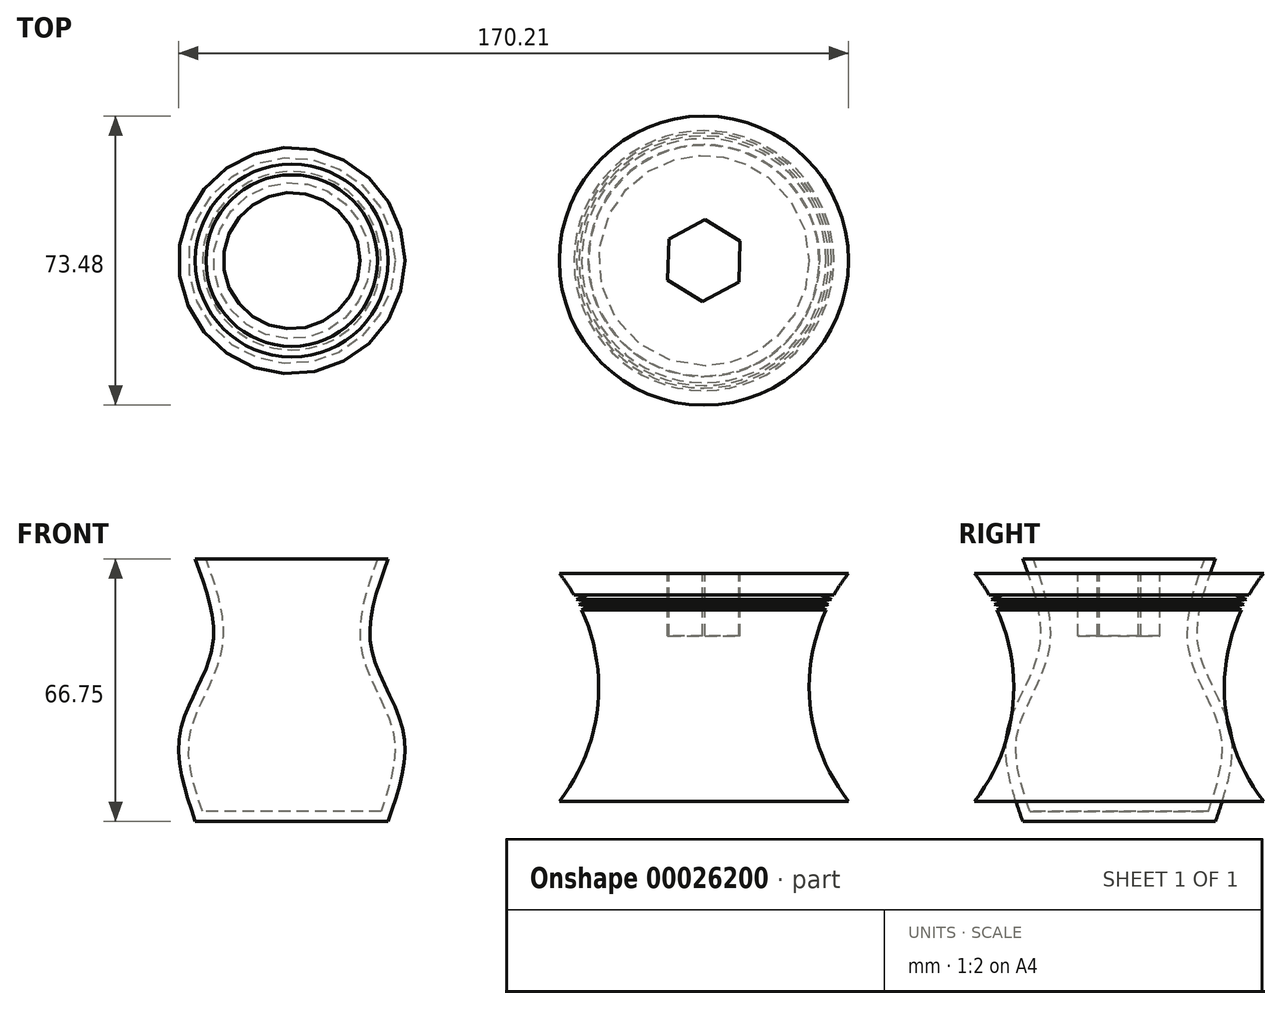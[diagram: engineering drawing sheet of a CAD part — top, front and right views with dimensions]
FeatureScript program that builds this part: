
annotation { "Feature Type Name" : "Feature", "Feature Type Description" : "" }
export const myFeature = defineFeature(function(context is Context, id is Id, definition is map)
    precondition{}
    {
        {
            var Q0;
            Q0=qCreatedBy(makeId("Front.planeOp"),FACE);
            var sketch = newSketch(context, id + "F0", { "sketchPlane" : qUnion([Q0])});
            skLineSegment(sketch, "E0", {"start": v(0, 26.32) * mm, "end": v(-36.74, 26.32) * mm});
            skLineSegment(sketch, "E1", {"start": v(0, -31.64) * mm, "end": v(-36.74, -31.64) * mm});
            skArc(sketch, "E2", {"start": v(-36.74, -31.64) * mm, "mid": v(-27.06, -8.13) * mm, "end": v(-31.04, 16.98) * mm});
            skLineSegment(sketch, "E3", {"start": v(-33.02, 20.82) * mm, "end": v(-29.45, 20.82) * mm});
            skLineSegment(sketch, "E4", {"start": v(-29.45, 20.82) * mm, "end": v(-32.4, 19.7) * mm});
            skLineSegment(sketch, "E5", {"start": v(-32.4, 19.7) * mm, "end": v(-29.45, 19.12) * mm});
            skLineSegment(sketch, "E6", {"start": v(-29.45, 19.12) * mm, "end": v(-31.7, 18.38) * mm});
            skLineSegment(sketch, "E7", {"start": v(-31.7, 18.38) * mm, "end": v(-29.26, 17.9) * mm});
            skLineSegment(sketch, "E8", {"start": v(-29.26, 17.9) * mm, "end": v(-31.04, 16.98) * mm});
            skArc(sketch, "E9.trimOffspring", {"start": v(-33.02, 20.82) * mm, "mid": v(-34.78, 23.64) * mm, "end": v(-36.74, 26.32) * mm});
            skLineSegment(sketch, "E10", {"start": v(0, 26.32) * mm, "end": v(0, -31.64) * mm});
            skSolve(sketch);
        }
        {
            var Q0;
            Q0 = qSketchRegion(id + "F0", true);
            var Q1;
            Q1=sQuery(id+"F0.wireOp",EDGE,"E10");
            revolve(context, id + "F1", {"entities" : qUnion([Q0]), "axis" : qUnion([Q1]), "revolveType" : RevolveType.FULL});
        }
        {
            var Q0;
            Q0=makeQuery(id+"F1.opRevolve","SWEPT_FACE",FACE,{"disambiguationData":[OSD([sQuery(id+"F0.wireOp",EDGE,"E0")])]});
            var sketch = newSketch(context, id + "F2", { "sketchPlane" : qUnion([Q0])});
            skCircle(sketch, "E11.cCircle", {"center": v(0, 0) * mm, "radius": 9.03 * mm, "construction": true});
            skLineSegment(sketch, "E11.0", {"start": v(-8.88, 5.48) * mm, "end": v(0.3, 10.43) * mm});
            skLineSegment(sketch, "E11.1", {"start": v(0.3, 10.43) * mm, "end": v(9.18, 4.95) * mm});
            skLineSegment(sketch, "E11.2", {"start": v(9.18, 4.95) * mm, "end": v(8.88, -5.48) * mm});
            skLineSegment(sketch, "E11.3", {"start": v(8.88, -5.48) * mm, "end": v(-0.3, -10.43) * mm});
            skLineSegment(sketch, "E11.4", {"start": v(-0.3, -10.43) * mm, "end": v(-9.18, -4.95) * mm});
            skLineSegment(sketch, "E11.5", {"start": v(-9.18, -4.95) * mm, "end": v(-8.88, 5.48) * mm});
            skPoint(sketch, "E11.0.midPoint", {"position": v(-4.29, 7.95) * mm});
            skSolve(sketch);
        }
        {
            var Q0;
            Q0 = qSketchRegion(id + "F2", true);
            extrude(context, id + "F3", {"entities" : qUnion([Q0]), "operationType" : NewBodyOperationType.REMOVE, "oppositeDirection" : true, "depth" : 15.88 * mm});
        }
        {
            var Q0;
            Q0=qCreatedBy(makeId("Front.planeOp"),FACE);
            var sketch = newSketch(context, id + "F4", { "sketchPlane" : qUnion([Q0])});
            skLineSegment(sketch, "E12", {"start": v(-129.2, 30) * mm, "end": v(-104.7, 30) * mm});
            skLineSegment(sketch, "E13", {"start": v(-129.2, -36.75) * mm, "end": v(-104.7, -36.75) * mm});
            skFitSpline(sketch, "E14", {"points": [v(-129.2, 30) * mm, v(-124.91, 7.34) * mm, v(-133.08, -14.1) * mm, v(-129.2, -36.75) * mm], "startDerivative": vector(25.23, -69.04) * mm, "endDerivative": vector(23.77, -69.17) * mm});
            skLineSegment(sketch, "E15", {"start": v(-104.7, 30) * mm, "end": v(-104.7, -36.75) * mm});
            skSolve(sketch);
        }
        {
            var Q0;
            Q0 = qSketchRegion(id + "F4", true);
            var Q1;
            Q1=sQuery(id+"F4.wireOp",EDGE,"E15");
            revolve(context, id + "F5", {"entities" : qUnion([Q0]), "axis" : qUnion([Q1]), "revolveType" : RevolveType.FULL});
        }
        {
            var Q0;
            Q0=makeQuery(id+"F5.opRevolve","SWEPT_FACE",FACE,{"disambiguationData":[OSD([sQuery(id+"F4.wireOp",EDGE,"E12")])]});
            shell(context, id + "F6", {"entities" : qUnion([Q0]), "thickness" : 2.54 * mm});
        }
    });
